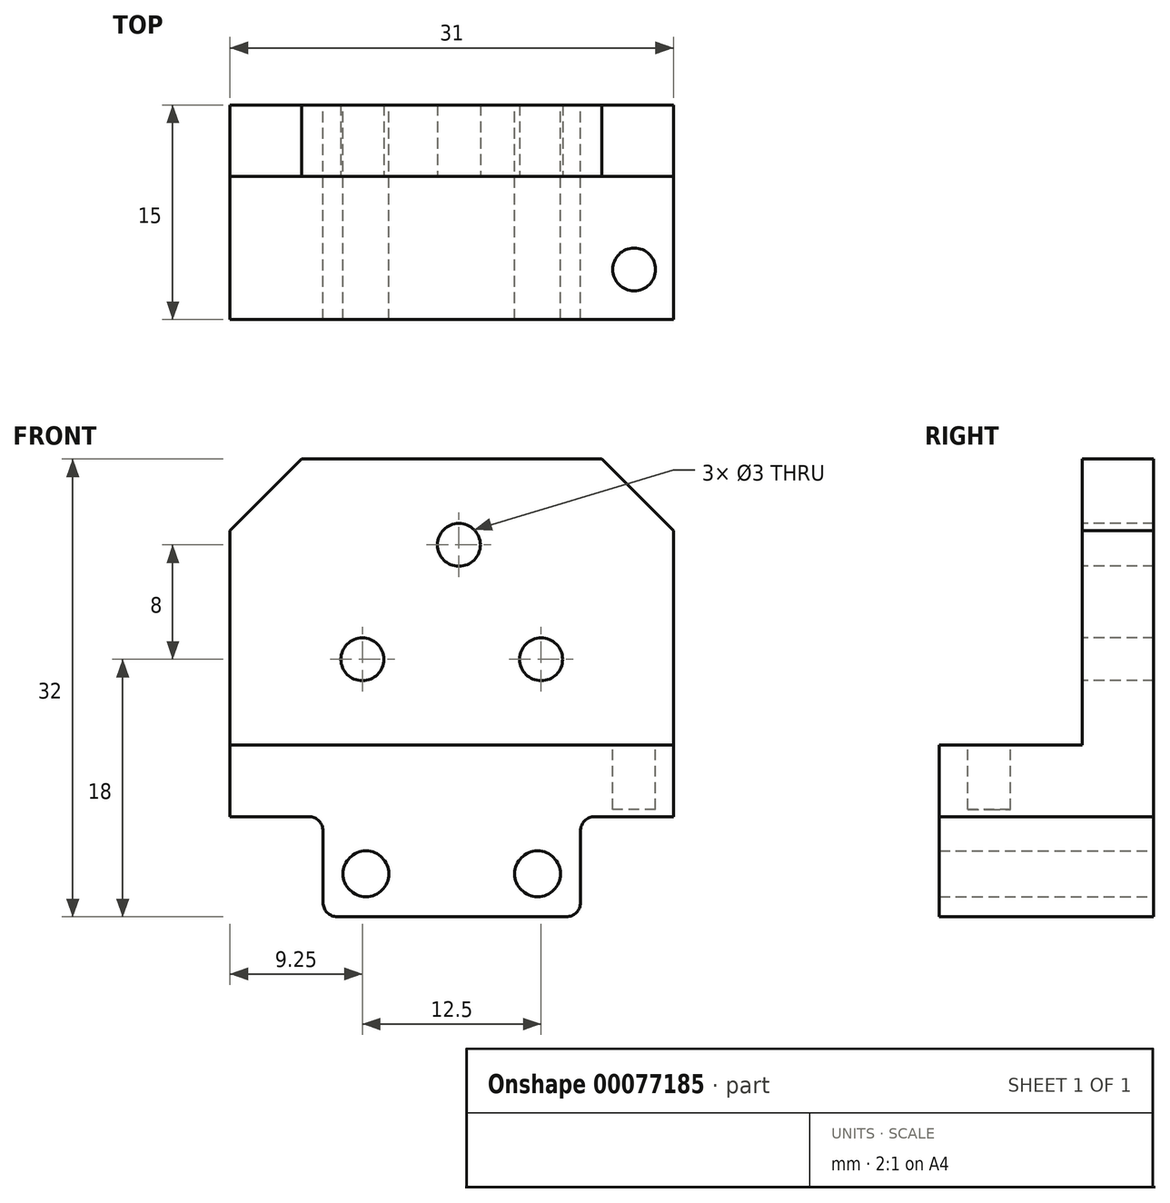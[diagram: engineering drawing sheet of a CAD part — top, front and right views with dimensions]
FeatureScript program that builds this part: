
annotation { "Feature Type Name" : "Feature", "Feature Type Description" : "" }
export const myFeature = defineFeature(function(context is Context, id is Id, definition is map)
    precondition{}
    {
        {
            var Q0;
            Q0=qCreatedBy(makeId("Front.planeOp"),FACE);
            var sketch = newSketch(context, id + "F0", { "sketchPlane" : qUnion([Q0])});
            skLineSegment(sketch, "E0.bottom", {"start": v(0, 0) * mm, "end": v(18, 0) * mm});
            skLineSegment(sketch, "E0.top", {"start": v(0, 7) * mm, "end": v(18, 7) * mm});
            skLineSegment(sketch, "E0.left", {"start": v(0, 0) * mm, "end": v(0, 7) * mm});
            skLineSegment(sketch, "E0.right", {"start": v(18, 0) * mm, "end": v(18, 7) * mm});
            skCircle(sketch, "E1", {"center": v(3, 3) * mm, "radius": 1.6 * mm});
            skCircle(sketch, "E2", {"center": v(15, 3) * mm, "radius": 1.6 * mm});
            skLineSegment(sketch, "E3", {"start": v(0, 12) * mm, "end": v(24.5, 12) * mm});
            skLineSegment(sketch, "E4", {"start": v(24.5, 12) * mm, "end": v(24.5, 7) * mm});
            skLineSegment(sketch, "E5", {"start": v(24.5, 7) * mm, "end": v(18, 7) * mm});
            skLineSegment(sketch, "E6", {"start": v(0, 7) * mm, "end": v(-6.5, 7) * mm});
            skLineSegment(sketch, "E7", {"start": v(-6.5, 7) * mm, "end": v(-6.5, 12) * mm});
            skLineSegment(sketch, "E8", {"start": v(-6.5, 12) * mm, "end": v(0, 12) * mm});
            skSolve(sketch);
        }
        {
            var Q0;
            Q0=qSketchRegion(id+"F0",true);
            extrude(context, id + "F1", {"entities" : qUnion([Q0]), "depth" : 15 * mm});
        }
        {
            var Q0;
            Q0=makeQuery(id+"F1.opExtrude","SWEPT_FACE",FACE,{"disambiguationData":[OSD([sQuery(id+"F0.wireOp",EDGE,"E3"),sQuery(id+"F0.wireOp",EDGE,"E8")])]});
            var sketch = newSketch(context, id + "F2", { "sketchPlane" : qUnion([Q0])});
            skLineSegment(sketch, "E9.bottom", {"start": v(-6.5, 0) * mm, "end": v(24.5, 0) * mm});
            skLineSegment(sketch, "E9.top", {"start": v(-6.5, -5) * mm, "end": v(24.5, -5) * mm});
            skLineSegment(sketch, "E9.left", {"start": v(-6.5, 0) * mm, "end": v(-6.5, -5) * mm});
            skLineSegment(sketch, "E9.right", {"start": v(24.5, 0) * mm, "end": v(24.5, -5) * mm});
            skSolve(sketch);
        }
        {
            var Q0;
            Q0=qSketchRegion(id+"F2",true);
            extrude(context, id + "F3", {"entities" : qUnion([Q0]), "operationType" : NewBodyOperationType.ADD, "depth" : 20 * mm});
        }
        {
            var Q0;
            Q0=makeQuery(id+"F3.opExtrude","SWEPT_FACE",FACE,{"disambiguationData":[OSD([sQuery(id+"F2.wireOp",EDGE,"E9.top")])]});
            var sketch = newSketch(context, id + "F4", { "sketchPlane" : qUnion([Q0])});
            skCircle(sketch, "E10", {"center": v(2.75, 18) * mm, "radius": 1.5 * mm});
            skCircle(sketch, "E11", {"center": v(15.25, 18) * mm, "radius": 1.5 * mm});
            skSolve(sketch);
        }
        {
            var Q0;
            Q0=qSketchRegion(id+"F4",true);
            extrude(context, id + "F5", {"entities" : qUnion([Q0]), "operationType" : NewBodyOperationType.REMOVE, "oppositeDirection" : true, "depth" : 25 * mm});
        }
        {
            var Q0;
            Q0=makeQuery(id+"F1.opExtrude","SWEPT_FACE",FACE,{"disambiguationData":[OSD([sQuery(id+"F0.wireOp",EDGE,"E3"),sQuery(id+"F0.wireOp",EDGE,"E8")])]});
            var sketch = newSketch(context, id + "F6", { "sketchPlane" : qUnion([Q0])});
            skCircle(sketch, "E12", {"center": v(21.75, -11.5) * mm, "radius": 1.5 * mm});
            skSolve(sketch);
        }
        {
            var Q0;
            Q0=qSketchRegion(id+"F6",true);
            extrude(context, id + "F7", {"entities" : qUnion([Q0]), "operationType" : NewBodyOperationType.REMOVE, "oppositeDirection" : true, "depth" : 4.5 * mm});
        }
        {
            var Q0;
            Q0=makeQuery(id+"F1.opExtrude","SWEPT_EDGE",EDGE,{"disambiguationData":[OSD([sQuery(id+"F0.wireOp",EDGE,"E0.bottom"),sQuery(id+"F0.wireOp",EDGE,"E0.left")])]});
            var Q1;
            Q1=makeQuery(id+"F1.opExtrude","SWEPT_EDGE",EDGE,{"disambiguationData":[OSD([sQuery(id+"F0.wireOp",EDGE,"E0.bottom"),sQuery(id+"F0.wireOp",EDGE,"E0.right")])]});
            var Q2;
            Q2=makeQuery(id+"F1.opExtrude","SWEPT_EDGE",EDGE,{"disambiguationData":[OSD([sQuery(id+"F0.wireOp",EDGE,"E0.top"),sQuery(id+"F0.wireOp",EDGE,"E0.left"),sQuery(id+"F0.wireOp",EDGE,"E6")])]});
            var Q3;
            Q3=makeQuery(id+"F1.opExtrude","SWEPT_EDGE",EDGE,{"disambiguationData":[OSD([sQuery(id+"F0.wireOp",EDGE,"E0.top"),sQuery(id+"F0.wireOp",EDGE,"E0.right"),sQuery(id+"F0.wireOp",EDGE,"E5")])]});
            fillet(context, id + "F8", {"entities" : qUnion([Q0, Q1, Q2, Q3]), "radius" : 1 * mm, "tangentPropagation" : true, "allowEdgeOverflow" : false});
        }
        {
            var Q0;
            Q0=makeQuery(id+"F3.opExtrude","CAP_EDGE",EDGE,{"disambiguationData":[OSD([sQuery(id+"F2.wireOp",EDGE,"E9.right")])],"isStart":false});
            var Q1;
            Q1=makeQuery(id+"F3.opExtrude","CAP_EDGE",EDGE,{"disambiguationData":[OSD([sQuery(id+"F2.wireOp",EDGE,"E9.left")])],"isStart":false});
            chamfer(context, id + "F9", {"entities" : qUnion([Q0, Q1]), "width" : 5 * mm, "tangentPropagation" : true});
        }
        {
            var Q0;
            Q0=makeQuery(id+"F3.opExtrude","SWEPT_FACE",FACE,{"disambiguationData":[OSD([sQuery(id+"F2.wireOp",EDGE,"E9.top")])]});
            var sketch = newSketch(context, id + "F10", { "sketchPlane" : qUnion([Q0])});
            skCircle(sketch, "E13", {"center": v(9.5, 26) * mm, "radius": 1.5 * mm});
            skSolve(sketch);
        }
        {
            var Q0;
            Q0=qSketchRegion(id+"F10",true);
            extrude(context, id + "F11", {"entities" : qUnion([Q0]), "operationType" : NewBodyOperationType.REMOVE, "oppositeDirection" : true, "depth" : 25 * mm});
        }
    });
